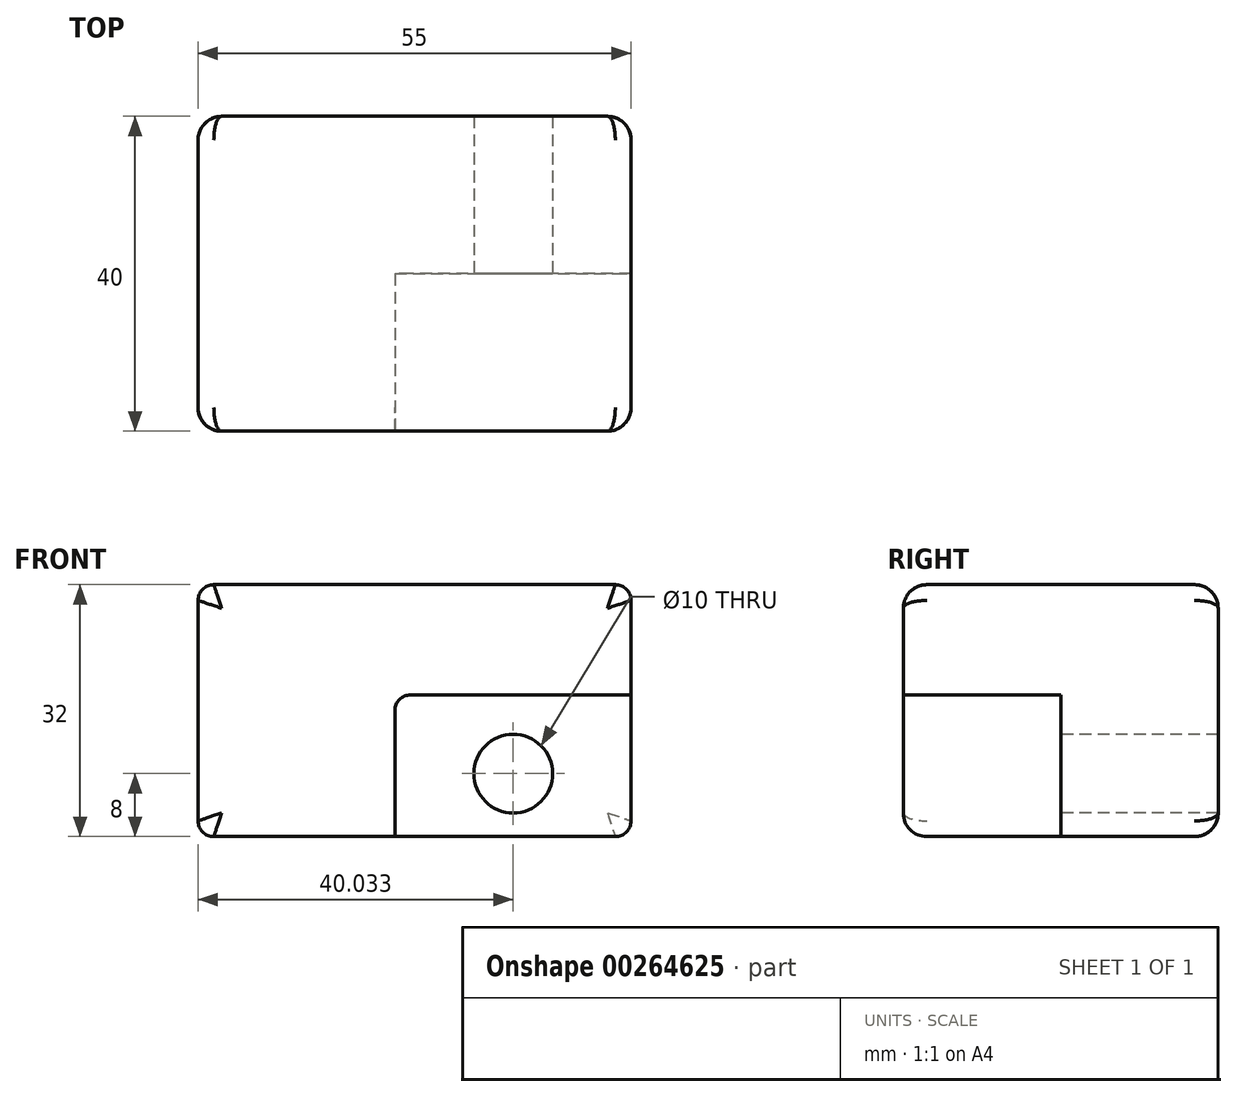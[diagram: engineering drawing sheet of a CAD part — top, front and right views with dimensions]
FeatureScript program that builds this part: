
annotation { "Feature Type Name" : "Feature", "Feature Type Description" : "" }
export const myFeature = defineFeature(function(context is Context, id is Id, definition is map)
    precondition{}
    {
        {
            var Q0;
            Q0=qCreatedBy(makeId("Front.planeOp"),FACE);
            var sketch = newSketch(context, id + "F0", { "sketchPlane" : qUnion([Q0])});
            skLineSegment(sketch, "E0.bottom", {"start": v(0, 0) * mm, "end": v(55, 0) * mm});
            skLineSegment(sketch, "E0.top", {"start": v(0, -32) * mm, "end": v(55, -32) * mm});
            skLineSegment(sketch, "E0.left", {"start": v(0, 0) * mm, "end": v(0, -32) * mm});
            skLineSegment(sketch, "E0.right", {"start": v(55, 0) * mm, "end": v(55, -32) * mm});
            skSolve(sketch);
        }
        {
            var Q0;
            Q0=makeQuery(id+"F0.imprint","IMPRINT",FACE,{"disambiguationData":[TD([[makeQuery(id+"F0.imprint","IMPRINT",EDGE,{"derivedFrom":sQuery(id+"F0.wireOp",EDGE,"E0.bottom")}),-1.0]])]});
            extrude(context, id + "F1", {"entities" : qUnion([Q0]), "depth" : 40 * mm});
        }
        {
            var Q0;
            Q0=makeQuery(id+"F1.opExtrude","CAP_FACE",FACE,{"disambiguationData":[OSD([sQuery(id+"F0.wireOp",EDGE,"E0.bottom"),sQuery(id+"F0.wireOp",EDGE,"E0.top"),sQuery(id+"F0.wireOp",EDGE,"E0.left"),sQuery(id+"F0.wireOp",EDGE,"E0.right")])],"isStart":false});
            var sketch = newSketch(context, id + "F2", { "sketchPlane" : qUnion([Q0])});
            skLineSegment(sketch, "E1.bottom", {"start": v(55, -32) * mm, "end": v(25, -32) * mm});
            skLineSegment(sketch, "E1.top", {"start": v(55, -14) * mm, "end": v(25, -14) * mm});
            skLineSegment(sketch, "E1.left", {"start": v(55, -32) * mm, "end": v(55, -14) * mm});
            skLineSegment(sketch, "E1.right", {"start": v(25, -32) * mm, "end": v(25, -14) * mm});
            skSolve(sketch);
        }
        {
            var Q0;
            Q0=makeQuery(id+"F2.imprint","IMPRINT",FACE,{"disambiguationData":[TD([[makeQuery(id+"F2.imprint","IMPRINT",EDGE,{"derivedFrom":sQuery(id+"F2.wireOp",EDGE,"E1.bottom")}),1.0]])]});
            extrude(context, id + "F3", {"entities" : qUnion([Q0]), "operationType" : NewBodyOperationType.REMOVE, "oppositeDirection" : true, "depth" : 20 * mm});
        }
        {
            var Q0;
            Q0=makeQuery(id+"F3.boolean.opBoolean","COPY",FACE,{"derivedFrom":makeQuery(id+"F3.opExtrude","CAP_FACE",FACE,{"disambiguationData":[OSD([sQuery(id+"F2.wireOp",EDGE,"E1.bottom"),sQuery(id+"F2.wireOp",EDGE,"E1.top"),sQuery(id+"F2.wireOp",EDGE,"E1.left"),sQuery(id+"F2.wireOp",EDGE,"E1.right")])],"isStart":false})});
            var sketch = newSketch(context, id + "F4", { "sketchPlane" : qUnion([Q0])});
            skCircle(sketch, "E2", {"center": v(40.03, -24) * mm, "radius": 5 * mm});
            skSolve(sketch);
        }
        {
            var Q0;
            Q0=makeQuery(id+"F4.imprint","IMPRINT",FACE,{"disambiguationData":[TD([[makeQuery(id+"F4.imprint","IMPRINT",EDGE,{"derivedFrom":sQuery(id+"F4.wireOp",EDGE,"E2")}),1.0]])]});
            extrude(context, id + "F5", {"entities" : qUnion([Q0]), "operationType" : NewBodyOperationType.REMOVE, "endBound" : BoundingType.THROUGH_ALL, "oppositeDirection" : true, "depth" : 10 * mm});
        }
        {
            var Q0;
            Q0=makeQuery(id+"F1.opExtrude","SWEPT_EDGE",EDGE,{"disambiguationData":[OSD([sQuery(id+"F0.wireOp",EDGE,"E0.top"),sQuery(id+"F0.wireOp",EDGE,"E0.left")])]});
            var Q1;
            Q1=makeQuery(id+"F3.boolean.opBoolean","COPY",EDGE,{"derivedFrom":makeQuery(id+"F3.opExtrude","SWEPT_EDGE",EDGE,{"disambiguationData":[OSD([sQuery(id+"F0.wireOp",EDGE,"E0.top"),sQuery(id+"F2.wireOp",EDGE,"E1.bottom"),sQuery(id+"F2.wireOp",EDGE,"E1.right")])]})});
            var Q2;
            Q2=makeQuery(id+"F3.boolean.opBoolean","COPY",EDGE,{"derivedFrom":makeQuery(id+"F3.opExtrude","SWEPT_EDGE",EDGE,{"disambiguationData":[OSD([sQuery(id+"F2.wireOp",EDGE,"E1.top"),sQuery(id+"F2.wireOp",EDGE,"E1.right")])]})});
            var Q3;
            Q3=makeQuery(id+"F3.boolean.opBoolean","COPY",EDGE,{"derivedFrom":makeQuery(id+"F3.opExtrude","SWEPT_EDGE",EDGE,{"disambiguationData":[OSD([sQuery(id+"F0.wireOp",EDGE,"E0.right"),sQuery(id+"F2.wireOp",EDGE,"E1.top"),sQuery(id+"F2.wireOp",EDGE,"E1.left")])]})});
            var Q4;
            Q4=makeQuery(id+"F1.opExtrude","SWEPT_EDGE",EDGE,{"disambiguationData":[OSD([sQuery(id+"F0.wireOp",EDGE,"E0.bottom"),sQuery(id+"F0.wireOp",EDGE,"E0.left")])]});
            var Q5;
            Q5=makeQuery(id+"F1.opExtrude","SWEPT_EDGE",EDGE,{"disambiguationData":[OSD([sQuery(id+"F0.wireOp",EDGE,"E0.bottom"),sQuery(id+"F0.wireOp",EDGE,"E0.right")])]});
            fillet(context, id + "F6", {"entities" : qUnion([Q0, Q1, Q2, Q3, Q4, Q5]), "radius" : 2 * mm, "tangentPropagation" : true, "allowEdgeOverflow" : false});
        }
        {
            var Q0;
            Q0=makeQuery(id+"F1.opExtrude","CAP_EDGE",EDGE,{"disambiguationData":[OSD([sQuery(id+"F0.wireOp",EDGE,"E0.top")])],"isStart":false});
            var Q1;
            Q1=makeQuery(id+"F1.opExtrude","CAP_EDGE",EDGE,{"disambiguationData":[OSD([sQuery(id+"F0.wireOp",EDGE,"E0.left")])],"isStart":false});
            var Q2;
            Q2=makeQuery(id+"F1.opExtrude","CAP_EDGE",EDGE,{"disambiguationData":[OSD([sQuery(id+"F0.wireOp",EDGE,"E0.bottom")])],"isStart":false});
            var Q3;
            Q3=makeQuery(id+"F3.boolean.opBoolean","COPY",EDGE,{"derivedFrom":makeQuery(id+"F3.opExtrude","CAP_EDGE",EDGE,{"disambiguationData":[OSD([sQuery(id+"F2.wireOp",EDGE,"E1.right")])],"isStart":true})});
            var Q4;
            Q4=makeQuery(id+"F3.boolean.opBoolean","COPY",EDGE,{"derivedFrom":makeQuery(id+"F3.opExtrude","CAP_EDGE",EDGE,{"disambiguationData":[OSD([sQuery(id+"F2.wireOp",EDGE,"E1.top")])],"isStart":true})});
            var Q5;
            Q5=makeQuery(id+"F1.opExtrude","CAP_EDGE",EDGE,{"disambiguationData":[OSD([sQuery(id+"F0.wireOp",EDGE,"E0.right")])],"isStart":false});
            fillet(context, id + "F7", {"entities" : qUnion([Q0, Q1, Q2, Q3, Q4, Q5]), "radius" : 3 * mm, "tangentPropagation" : true, "allowEdgeOverflow" : false});
        }
        {
            var Q0;
            Q0=makeQuery(id+"F3.boolean.opBoolean","COPY",EDGE,{"derivedFrom":makeQuery(id+"F3.opExtrude","CAP_EDGE",EDGE,{"disambiguationData":[OSD([sQuery(id+"F2.wireOp",EDGE,"E1.bottom")])],"isStart":false})});
            var Q1;
            Q1=makeQuery(id+"F3.boolean.opBoolean","COPY",EDGE,{"derivedFrom":makeQuery(id+"F3.opExtrude","CAP_EDGE",EDGE,{"disambiguationData":[OSD([sQuery(id+"F2.wireOp",EDGE,"E1.left")])],"isStart":false})});
            var Q2;
            Q2=makeQuery(id+"F1.opExtrude","SWEPT_EDGE",EDGE,{"disambiguationData":[OSD([sQuery(id+"F0.wireOp",EDGE,"E0.top"),sQuery(id+"F0.wireOp",EDGE,"E0.right")])]});
            fillet(context, id + "F8", {"entities" : qUnion([Q0, Q1, Q2]), "radius" : 2 * mm, "tangentPropagation" : true, "allowEdgeOverflow" : false});
        }
        {
            var Q0;
            Q0=makeQuery(id+"F1.opExtrude","CAP_EDGE",EDGE,{"disambiguationData":[OSD([sQuery(id+"F0.wireOp",EDGE,"E0.top")])],"isStart":true});
            var Q1;
            Q1=makeQuery(id+"F1.opExtrude","CAP_EDGE",EDGE,{"disambiguationData":[OSD([sQuery(id+"F0.wireOp",EDGE,"E0.right")])],"isStart":true});
            var Q2;
            Q2=makeQuery(id+"F1.opExtrude","CAP_EDGE",EDGE,{"disambiguationData":[OSD([sQuery(id+"F0.wireOp",EDGE,"E0.bottom")])],"isStart":true});
            var Q3;
            Q3=makeQuery(id+"F1.opExtrude","CAP_EDGE",EDGE,{"disambiguationData":[OSD([sQuery(id+"F0.wireOp",EDGE,"E0.left")])],"isStart":true});
            fillet(context, id + "F9", {"entities" : qUnion([Q0, Q1, Q2, Q3]), "radius" : 3 * mm, "tangentPropagation" : true, "allowEdgeOverflow" : false});
        }
    });
